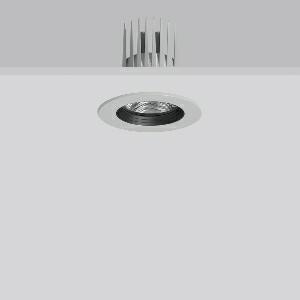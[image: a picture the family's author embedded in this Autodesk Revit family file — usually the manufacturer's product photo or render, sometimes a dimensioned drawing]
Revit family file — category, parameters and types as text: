
# Revit family: heledon_mini_e_901741_004_3_7ad0
name_source: partatom
category: Lighting Fixtures
units: mm (PartAtom-declared; Revit-internal decimal feet)

## family parameters
Cut with Voids When Loaded = No
Host = Face
Light Source = No
Part Type = Normal
Room Calculation Point = No
Round Connector Dimension = Use Diameter
Shared = No

## types (1)
- HELEDON mini E (1 x LED Modul 935, 2500 lm, 3500)
    Apparent Load = 20 VA
    Approval mark = CE
    CIE Flux Codes = 99 100 100 100 100
    Color Rendering = 92
    Color Temperature = 3500
    Default Elevation = 1800 mm
    Description = Series: HELEDON mini
Round recessed downlight. Housing: die-cast aluminium, powder-coated. Black plastic ring and recessed LED to prevent glare from the side. Optical assembly with reflector made of MIRO-Silver with 98% total light reflection for outstanding efficiency - can be changed without tools. Best colour rendering index Ra>90. Suitable for Recessed ceiling mounting. Installation without tools thanks to spring fastening system. Including separate LED converter with connecting cable 600 mm.High quality converter without flickering and stroboscopic effect. Through-wiring box (5 pole) available as accessory. The following accessories can be mounted without use of tools: interchangeable lenses, decorative glasses, honeycomb louvre, clear and frosted diffusers, white interchangeable plastic ring. 
Colour: silver
Diameter: 124 mm
Height: 3 mm
Cut-out diameter: 114 mm
Recess height: 170 mm
Luminaire: recess height: 120 mm
Lamp: LED
Socket: without socket
Colour temperature: 3500K
Colour rendering index (CRI): 92
System power: 20 W
Rated luminous flux: 2500 lm
Luminous efficiency: 125 lm/W
Control gear: Regulated power supply
Protection class: II
Type of protection: IP 20
    Height = 0 mm  [stored 0 ft]
    Lamp = 1 x LED Modul 935
    Lamp Light Flux = 2500 lm
    Lamp count = 1
    Length = 124 mm  [stored 0.406824 ft]
    Lifetime = 50000 h
    Luminous efficacy = 125 lm/W
    Manufacturer = RZB
    ModVariant = No
    Model = 901741.004.3
    Mounting Place = Ceiling
    Mounting Type = Recessed
    Number of Poles = 1
    OnlyDefault = Yes
    Power Factor = 1
    Product Name = HELEDON mini E
    Product group = Recessed downlights
    ProductGroupID = 402
    Protection Class = Protection class II
    Protection Degree = IP 20
    RLX_Detail_Level = 1
    RLX_Emergency_Light_Flux = 0 lm
    RLX_Emergency_Type = 0
    RLX_Emergency_Type_DB = No
    RlxData = <blob elided: 128029 chars, md5=0f8aa558>
    Socket = socket
    Standby Power = 0 W
    System Light Flux = 2500 lm
    System Power = 20 W
    Type Comments = Product without accessories
    Type Image = 901657.004.jpg
    URL = http://relux.com
    VarID = ---
    Voltage = 230 V
    Voltage Range = 220-240 V
    Weight = 0.00 kg
    Width = 0 mm  [stored 0 ft]

note: [stored X ft] marks values corroborated as IEEE doubles in the binary element streams (Revit-internal decimal feet)

## geometry (parser evidence)
native form markers: Blend x4, Sweep x12
no freeform markers — native parametric forms only
